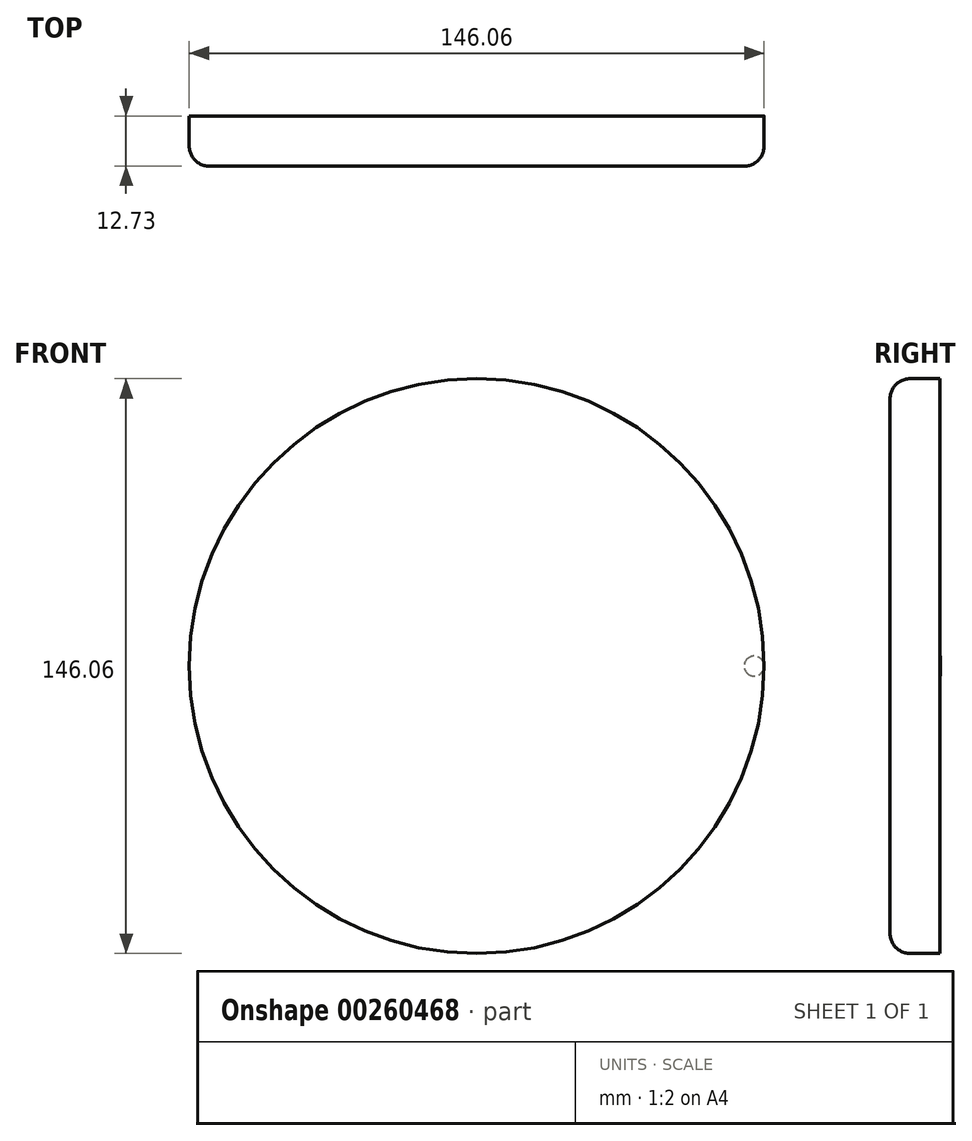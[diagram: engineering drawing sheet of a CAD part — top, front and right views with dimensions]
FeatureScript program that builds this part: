
annotation { "Feature Type Name" : "Feature", "Feature Type Description" : "" }
export const myFeature = defineFeature(function(context is Context, id is Id, definition is map)
    precondition{}
    {
        {
            var Q0;
            Q0=qCreatedBy(makeId("Front.planeOp"),FACE);
            var sketch = newSketch(context, id + "F0", { "sketchPlane" : qUnion([Q0])});
            skCircle(sketch, "E0", {"center": v(0, 0) * mm, "radius": 73.02 * mm});
            skSolve(sketch);
        }
        {
            var Q0;
            Q0=makeQuery(id+"F0.imprint","IMPRINT",FACE,{"disambiguationData":[TD([[makeQuery(id+"F0.imprint","IMPRINT",EDGE,{"derivedFrom":sQuery(id+"F0.wireOp",EDGE,"E0")}),1.0]])]});
            extrude(context, id + "F1", {"entities" : qUnion([Q0]), "depth" : 12.7 * mm});
        }
        {
            var Q0;
            Q0=makeQuery(id+"F1.opExtrude","CAP_EDGE",EDGE,{"disambiguationData":[OSD([sQuery(id+"F0.wireOp",EDGE,"E0")])],"isStart":false});
            fillet(context, id + "F2", {"entities" : qUnion([Q0]), "radius" : 5.08 * mm, "tangentPropagation" : true, "allowEdgeOverflow" : false});
        }
        {
            var Q0;
            Q0=makeQuery(id+"F1.opExtrude","CAP_FACE",FACE,{"disambiguationData":[OSD([sQuery(id+"F0.wireOp",EDGE,"E0")])],"isStart":true});
            var sketch = newSketch(context, id + "F3", { "sketchPlane" : qUnion([Q0])});
            skLineSegment(sketch, "E1", {"start": v(-73.02, 0) * mm, "end": v(-70.48, 0) * mm});
            skCircle(sketch, "E2", {"center": v(-70.48, 0) * mm, "radius": 2.54 * mm});
            skSolve(sketch);
        }
        {
            var Q0;
            Q0=makeQuery(id+"F3.imprint","IMPRINT",FACE,{"disambiguationData":[TD([[makeQuery(id+"F3.imprint","IMPRINT",EDGE,{"derivedFrom":sQuery(id+"F3.wireOp",EDGE,"E2")}),1.0]])]});
            extrude(context, id + "F4", {"entities" : qUnion([Q0]), "operationType" : NewBodyOperationType.ADD, "depth" : 0.03 * mm});
        }
    });
